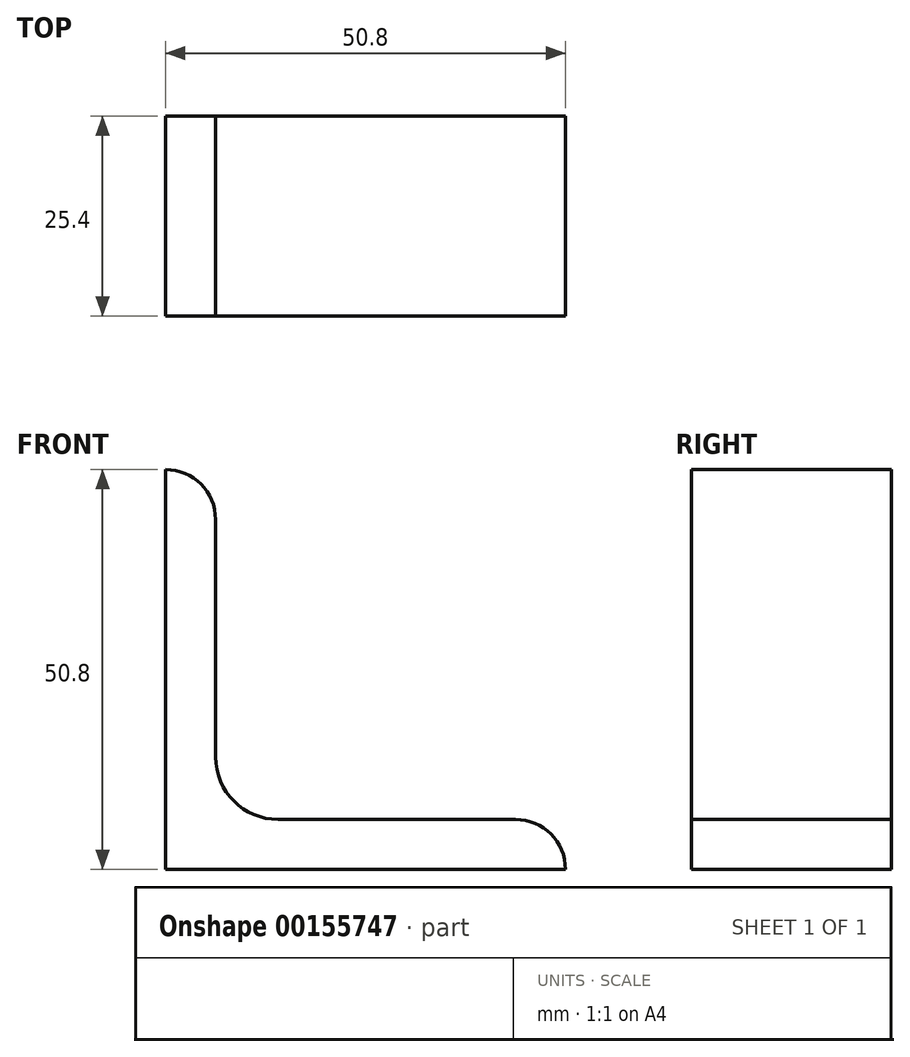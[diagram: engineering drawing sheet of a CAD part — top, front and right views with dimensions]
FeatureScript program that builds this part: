
annotation { "Feature Type Name" : "Feature", "Feature Type Description" : "" }
export const myFeature = defineFeature(function(context is Context, id is Id, definition is map)
    precondition{}
    {
        {
            var Q0;
            Q0=qCreatedBy(makeId("Front.planeOp"),FACE);
            var sketch = newSketch(context, id + "F0", { "sketchPlane" : qUnion([Q0])});
            skLineSegment(sketch, "E0", {"start": v(0, 50.8) * mm, "end": v(0, 0) * mm});
            skLineSegment(sketch, "E1", {"start": v(0, 0) * mm, "end": v(50.8, 0) * mm});
            skLineSegment(sketch, "E2", {"start": v(50.8, 0) * mm, "end": v(50.8, 6.35) * mm});
            skLineSegment(sketch, "E3", {"start": v(50.8, 6.35) * mm, "end": v(6.35, 6.35) * mm});
            skLineSegment(sketch, "E4", {"start": v(6.35, 6.35) * mm, "end": v(6.35, 50.8) * mm});
            skLineSegment(sketch, "E5", {"start": v(6.35, 50.8) * mm, "end": v(0, 50.8) * mm});
            skSolve(sketch);
        }
        {
            var Q0;
            Q0 = qSketchRegion(id + "F0", true);
            extrude(context, id + "F1", {"entities" : qUnion([Q0]), "depth" : 25.4 * mm, "symmetric" : true});
        }
        {
            var Q0;
            Q0=makeQuery(id+"F1.opExtrude","SWEPT_EDGE",EDGE,{"disambiguationData":[OSD([sQuery(id+"F0.wireOp",EDGE,"E4"),sQuery(id+"F0.wireOp",EDGE,"E5")])]});
            var Q1;
            Q1=makeQuery(id+"F1.opExtrude","SWEPT_EDGE",EDGE,{"disambiguationData":[OSD([sQuery(id+"F0.wireOp",EDGE,"E2"),sQuery(id+"F0.wireOp",EDGE,"E3")])]});
            fillet(context, id + "F2", {"entities" : qUnion([Q0, Q1]), "radius" : 6.35 * mm, "tangentPropagation" : true, "allowEdgeOverflow" : false});
        }
        {
            var Q0;
            Q0=makeQuery(id+"F1.opExtrude","SWEPT_EDGE",EDGE,{"disambiguationData":[OSD([sQuery(id+"F0.wireOp",EDGE,"E3"),sQuery(id+"F0.wireOp",EDGE,"E4")])]});
            fillet(context, id + "F3", {"entities" : qUnion([Q0]), "radius" : 7.94 * mm, "tangentPropagation" : true, "allowEdgeOverflow" : false});
        }
    });
